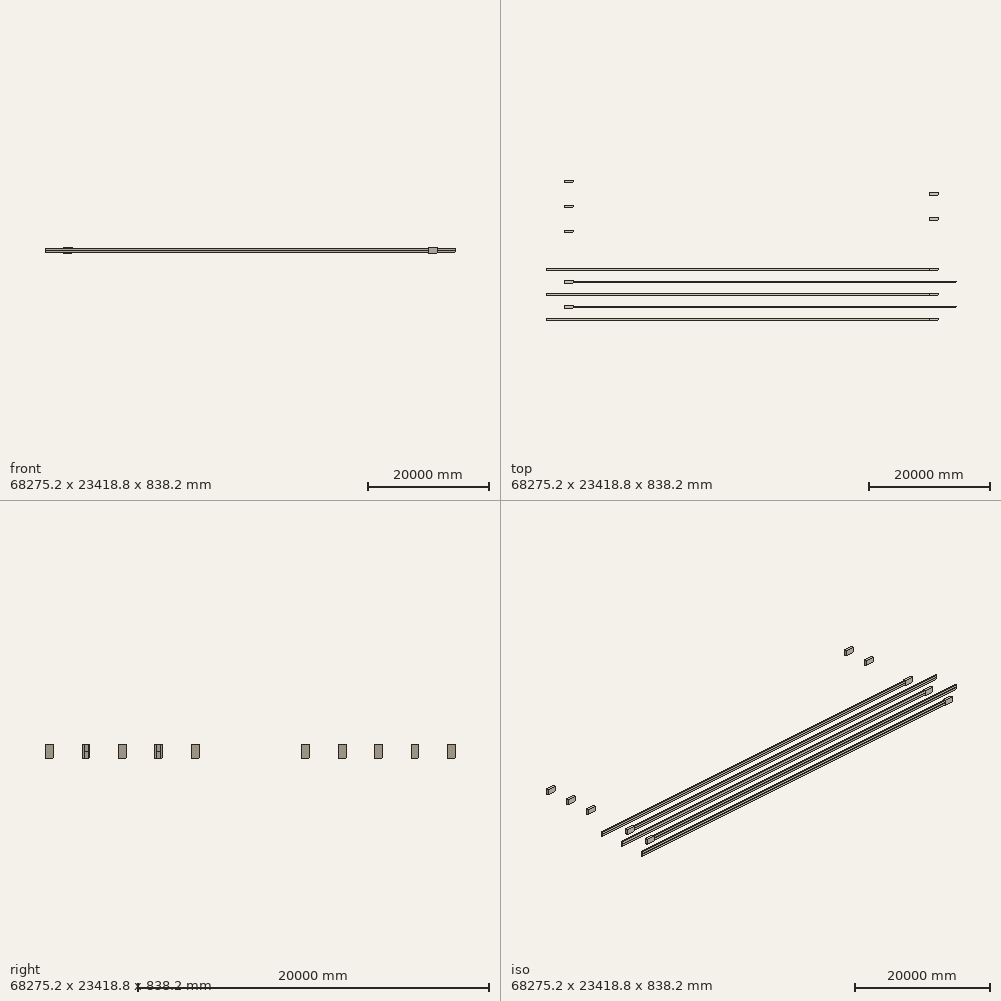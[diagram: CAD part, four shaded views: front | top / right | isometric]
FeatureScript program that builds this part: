
annotation { "Feature Type Name" : "Feature", "Feature Type Description" : "" }
export const myFeature = defineFeature(function(context is Context, id is Id, definition is map)
    precondition{}
    {
        {
            var Q0;
            Q0=qCreatedBy(makeId("Top.planeOp"),FACE);
            var sketch = newSketch(context, id + "F0", { "sketchPlane" : qUnion([Q0])});
            skLineSegment(sketch, "E0.bottom", {"start": v(-34137.6, 13411.2) * mm, "end": v(34137.6, 13411.2) * mm});
            skLineSegment(sketch, "E0.top", {"start": v(-34137.6, -13411.2) * mm, "end": v(34137.6, -13411.2) * mm});
            skLineSegment(sketch, "E0.left", {"start": v(-34137.6, 13411.2) * mm, "end": v(-34137.6, -13411.2) * mm});
            skLineSegment(sketch, "E0.right", {"start": v(34137.6, 13411.2) * mm, "end": v(34137.6, -13411.2) * mm});
            skPoint(sketch, "E0.middle", {"position": v(0, 0) * mm});
            skLineSegment(sketch, "E1", {"start": v(-31699.2, 13411.2) * mm, "end": v(-31699.2, 1219.2) * mm});
            skLineSegment(sketch, "E2", {"start": v(31699.2, 13411.2) * mm, "end": v(31699.2, 1219.2) * mm});
            skLineSegment(sketch, "E3", {"start": v(-31699.2, 1219.2) * mm, "end": v(-2438.4, 1219.2) * mm});
            skLineSegment(sketch, "E4", {"start": v(-31699.2, -1219.2) * mm, "end": v(-2438.4, -1219.2) * mm});
            skLineSegment(sketch, "E5", {"start": v(-2438.4, 13411.2) * mm, "end": v(-2438.4, 1219.2) * mm});
            skLineSegment(sketch, "E6", {"start": v(2438.4, 13411.2) * mm, "end": v(2438.4, 1219.2) * mm});
            skLineSegment(sketch, "E7.trimOffspring", {"start": v(-2438.4, -1219.2) * mm, "end": v(-2438.4, -13411.2) * mm});
            skLineSegment(sketch, "E8.trimOffspring", {"start": v(2438.4, 1219.2) * mm, "end": v(31699.2, 1219.2) * mm});
            skLineSegment(sketch, "E9.trimOffspring", {"start": v(2438.4, -1219.2) * mm, "end": v(31699.2, -1219.2) * mm});
            skLineSegment(sketch, "E10.trimOffspring", {"start": v(2438.4, -1219.2) * mm, "end": v(2438.4, -13411.2) * mm});
            skLineSegment(sketch, "E11.trimOffspring", {"start": v(-31699.2, -1219.2) * mm, "end": v(-31699.2, -13411.2) * mm});
            skLineSegment(sketch, "E12.trimOffspring", {"start": v(31699.2, -1219.2) * mm, "end": v(31699.2, -13411.2) * mm});
            skSolve(sketch);
        }
        {
            var Q0;
            {var subQ0=sQuery(id+"F0.wireOp",EDGE,"E1");Q0=makeQuery(id+"F0.imprint","IMPRINT",FACE,{"disambiguationData":[TD([[makeQuery(id+"F0.imprint","IMPRINT",EDGE,{"derivedFrom":subQ0}),1.0]])]});}
            var sketch = newSketch(context, id + "F1", { "sketchPlane" : qUnion([Q0])});
            skLineSegment(sketch, "E13.bottom", {"start": v(-31089.6, 2921) * mm, "end": v(-29616.4, 2921) * mm});
            skLineSegment(sketch, "E13.top", {"start": v(-31089.6, 3352.8) * mm, "end": v(-29616.4, 3352.8) * mm});
            skLineSegment(sketch, "E13.left", {"start": v(-31089.6, 2921) * mm, "end": v(-31089.6, 3352.8) * mm});
            skLineSegment(sketch, "E13.right", {"start": v(-29616.4, 2921) * mm, "end": v(-29616.4, 3352.8) * mm});
            skLineSegment(sketch, "E14.bottom", {"start": v(-31089.6, 7099.3) * mm, "end": v(-29616.4, 7099.3) * mm});
            skLineSegment(sketch, "E14.top", {"start": v(-31089.6, 7531.1) * mm, "end": v(-29616.4, 7531.1) * mm});
            skLineSegment(sketch, "E14.left", {"start": v(-31089.6, 7099.3) * mm, "end": v(-31089.6, 7531.1) * mm});
            skLineSegment(sketch, "E14.right", {"start": v(-29616.4, 7099.3) * mm, "end": v(-29616.4, 7531.1) * mm});
            skLineSegment(sketch, "E15.bottom", {"start": v(-31089.6, 11277.6) * mm, "end": v(-29616.4, 11277.6) * mm});
            skLineSegment(sketch, "E15.top", {"start": v(-31089.6, 11709.4) * mm, "end": v(-29616.4, 11709.4) * mm});
            skLineSegment(sketch, "E15.left", {"start": v(-31089.6, 11277.6) * mm, "end": v(-31089.6, 11709.4) * mm});
            skLineSegment(sketch, "E15.right", {"start": v(-29616.4, 11277.6) * mm, "end": v(-29616.4, 11709.4) * mm});
            skLineSegment(sketch, "E16.bottom", {"start": v(-31089.6, -9169.4) * mm, "end": v(-29616.4, -9169.4) * mm});
            skLineSegment(sketch, "E16.top", {"start": v(-31089.6, -9601.2) * mm, "end": v(-29616.4, -9601.2) * mm});
            skLineSegment(sketch, "E16.left", {"start": v(-31089.6, -9169.4) * mm, "end": v(-31089.6, -9601.2) * mm});
            skLineSegment(sketch, "E16.right", {"start": v(-29616.4, -9169.4) * mm, "end": v(-29616.4, -9601.2) * mm});
            skPoint(sketch, "E17.left.start.orphan", {"position": v(-31089.6, -5029.2) * mm});
            skLineSegment(sketch, "E18.bottom", {"start": v(-31089.6, -5029.2) * mm, "end": v(-29616.4, -5029.2) * mm});
            skLineSegment(sketch, "E18.top", {"start": v(-31089.6, -5461) * mm, "end": v(-29616.4, -5461) * mm});
            skLineSegment(sketch, "E18.left", {"start": v(-31089.6, -5029.2) * mm, "end": v(-31089.6, -5461) * mm});
            skLineSegment(sketch, "E18.right", {"start": v(-29616.4, -5029.2) * mm, "end": v(-29616.4, -5461) * mm});
            skLineSegment(sketch, "E19.bottom", {"start": v(31089.6, -7531.1) * mm, "end": v(29616.4, -7531.1) * mm});
            skLineSegment(sketch, "E19.top", {"start": v(31089.6, -7099.3) * mm, "end": v(29616.4, -7099.3) * mm});
            skLineSegment(sketch, "E19.left", {"start": v(31089.6, -7531.1) * mm, "end": v(31089.6, -7099.3) * mm});
            skLineSegment(sketch, "E19.right", {"start": v(29616.4, -7531.1) * mm, "end": v(29616.4, -7099.3) * mm});
            skLineSegment(sketch, "E20.bottom", {"start": v(31089.6, -11709.4) * mm, "end": v(29616.4, -11709.4) * mm});
            skLineSegment(sketch, "E20.top", {"start": v(31089.6, -11277.6) * mm, "end": v(29616.4, -11277.6) * mm});
            skLineSegment(sketch, "E20.left", {"start": v(31089.6, -11709.4) * mm, "end": v(31089.6, -11277.6) * mm});
            skLineSegment(sketch, "E20.right", {"start": v(29616.4, -11709.4) * mm, "end": v(29616.4, -11277.6) * mm});
            skLineSegment(sketch, "E21.bottom", {"start": v(31089.6, -3352.8) * mm, "end": v(29616.4, -3352.8) * mm});
            skLineSegment(sketch, "E21.top", {"start": v(31089.6, -2921) * mm, "end": v(29616.4, -2921) * mm});
            skLineSegment(sketch, "E21.left", {"start": v(31089.6, -3352.8) * mm, "end": v(31089.6, -2921) * mm});
            skLineSegment(sketch, "E21.right", {"start": v(29616.4, -3352.8) * mm, "end": v(29616.4, -2921) * mm});
            skPoint(sketch, "E22.oppositeSnap0", {"position": v(29616.4, -3136.9) * mm});
            skLineSegment(sketch, "E22.bottom", {"start": v(31089.6, 5029.2) * mm, "end": v(29616.4, 5029.2) * mm});
            skLineSegment(sketch, "E22.top", {"start": v(31089.6, 5461) * mm, "end": v(29616.4, 5461) * mm});
            skLineSegment(sketch, "E22.left", {"start": v(31089.6, 5029.2) * mm, "end": v(31089.6, 5461) * mm});
            skLineSegment(sketch, "E22.right", {"start": v(29616.4, 5029.2) * mm, "end": v(29616.4, 5461) * mm});
            skLineSegment(sketch, "E23.bottom", {"start": v(31089.6, 9169.4) * mm, "end": v(29616.4, 9169.4) * mm});
            skLineSegment(sketch, "E23.top", {"start": v(31089.6, 9601.2) * mm, "end": v(29616.4, 9601.2) * mm});
            skLineSegment(sketch, "E23.left", {"start": v(31089.6, 9169.4) * mm, "end": v(31089.6, 9601.2) * mm});
            skLineSegment(sketch, "E23.right", {"start": v(29616.4, 9169.4) * mm, "end": v(29616.4, 9601.2) * mm});
            skSolve(sketch);
        }
        {
            var Q0;
            Q0 = qSketchRegion(id + "F1", true);
            extrude(context, id + "F2", {"entities" : qUnion([Q0]), "depth" : 838.2 * mm, "offsetDistance" : 25.4 * mm});
        }
        {
            var Q0;
            Q0=makeQuery(id+"F2.opExtrude","SWEPT_FACE",FACE,{"disambiguationData":[OSD([sQuery(id+"F1.wireOp",EDGE,"E16.right")])]});
            var sketch = newSketch(context, id + "F3", { "sketchPlane" : qUnion([Q0])});
            skLineSegment(sketch, "E24.bottom", {"start": v(-9271, 42.33) * mm, "end": v(-9499.6, 42.33) * mm});
            skLineSegment(sketch, "E24.top", {"start": v(-9271, 397.93) * mm, "end": v(-9499.6, 397.93) * mm});
            skLineSegment(sketch, "E24.left", {"start": v(-9271, 42.33) * mm, "end": v(-9271, 397.93) * mm});
            skLineSegment(sketch, "E24.right", {"start": v(-9499.6, 42.33) * mm, "end": v(-9499.6, 397.93) * mm});
            skPoint(sketch, "E24.middle", {"position": v(-9385.3, 220.13) * mm});
            skPoint(sketch, "E24.middle.positionSnap0", {"position": v(-9385.3, 0) * mm});
            skPoint(sketch, "E24.centerSnap0", {"position": v(-9385.3, 0) * mm});
            skLineSegment(sketch, "E25.bottom", {"start": v(-9499.6, 440.27) * mm, "end": v(-9271, 440.27) * mm});
            skLineSegment(sketch, "E25.top", {"start": v(-9499.6, 795.87) * mm, "end": v(-9271, 795.87) * mm});
            skLineSegment(sketch, "E25.left", {"start": v(-9499.6, 440.27) * mm, "end": v(-9499.6, 795.87) * mm});
            skLineSegment(sketch, "E25.right", {"start": v(-9271, 440.27) * mm, "end": v(-9271, 795.87) * mm});
            skPoint(sketch, "E25.middle", {"position": v(-9385.3, 618.07) * mm});
            skLineSegment(sketch, "E26.bottom", {"start": v(-5359.4, 397.93) * mm, "end": v(-5130.8, 397.93) * mm});
            skLineSegment(sketch, "E26.top", {"start": v(-5359.4, 42.33) * mm, "end": v(-5130.8, 42.33) * mm});
            skLineSegment(sketch, "E26.left", {"start": v(-5359.4, 397.93) * mm, "end": v(-5359.4, 42.33) * mm});
            skLineSegment(sketch, "E26.right", {"start": v(-5130.8, 397.93) * mm, "end": v(-5130.8, 42.33) * mm});
            skPoint(sketch, "E26.middle", {"position": v(-5245.1, 220.13) * mm});
            skLineSegment(sketch, "E27.bottom", {"start": v(-5359.4, 440.27) * mm, "end": v(-5130.8, 440.27) * mm});
            skLineSegment(sketch, "E27.top", {"start": v(-5359.4, 795.87) * mm, "end": v(-5130.8, 795.87) * mm});
            skLineSegment(sketch, "E27.left", {"start": v(-5359.4, 440.27) * mm, "end": v(-5359.4, 795.87) * mm});
            skLineSegment(sketch, "E27.right", {"start": v(-5130.8, 440.27) * mm, "end": v(-5130.8, 795.87) * mm});
            skPoint(sketch, "E27.middle", {"position": v(-5245.1, 618.07) * mm});
            skSolve(sketch);
        }
        {
            var Q0;
            Q0 = qSketchRegion(id + "F3", true);
            extrude(context, id + "F4", {"entities" : qUnion([Q0]), "depth" : 63754 * mm, "offsetDistance" : 25.4 * mm});
        }
        {
            var Q0;
            Q0=makeQuery(id+"F2.opExtrude","SWEPT_FACE",FACE,{"disambiguationData":[OSD([sQuery(id+"F1.wireOp",EDGE,"E21.right")])]});
            var sketch = newSketch(context, id + "F5", { "sketchPlane" : qUnion([Q0])});
            skLineSegment(sketch, "E28.bottom", {"start": v(3022.6, 397.93) * mm, "end": v(3251.2, 397.93) * mm});
            skLineSegment(sketch, "E28.top", {"start": v(3022.6, 42.33) * mm, "end": v(3251.2, 42.33) * mm});
            skLineSegment(sketch, "E28.left", {"start": v(3022.6, 397.93) * mm, "end": v(3022.6, 42.33) * mm});
            skLineSegment(sketch, "E28.right", {"start": v(3251.2, 397.93) * mm, "end": v(3251.2, 42.33) * mm});
            skPoint(sketch, "E28.middle", {"position": v(3136.9, 220.13) * mm});
            skPoint(sketch, "E28.middle.positionSnap0", {"position": v(3136.9, 0) * mm});
            skPoint(sketch, "E28.centerSnap0", {"position": v(3136.9, 0) * mm});
            skLineSegment(sketch, "E29.bottom", {"start": v(3022.6, 440.27) * mm, "end": v(3251.2, 440.27) * mm});
            skLineSegment(sketch, "E29.top", {"start": v(3022.6, 795.87) * mm, "end": v(3251.2, 795.87) * mm});
            skLineSegment(sketch, "E29.left", {"start": v(3022.6, 440.27) * mm, "end": v(3022.6, 795.87) * mm});
            skLineSegment(sketch, "E29.right", {"start": v(3251.2, 440.27) * mm, "end": v(3251.2, 795.87) * mm});
            skPoint(sketch, "E29.middle", {"position": v(3136.9, 618.07) * mm});
            skLineSegment(sketch, "E30.bottom", {"start": v(7200.9, 397.93) * mm, "end": v(7429.5, 397.93) * mm});
            skLineSegment(sketch, "E30.top", {"start": v(7200.9, 42.33) * mm, "end": v(7429.5, 42.33) * mm});
            skLineSegment(sketch, "E30.left", {"start": v(7200.9, 397.93) * mm, "end": v(7200.9, 42.33) * mm});
            skLineSegment(sketch, "E30.right", {"start": v(7429.5, 397.93) * mm, "end": v(7429.5, 42.33) * mm});
            skPoint(sketch, "E30.middle", {"position": v(7315.2, 220.13) * mm});
            skLineSegment(sketch, "E31.bottom", {"start": v(7200.9, 795.87) * mm, "end": v(7429.5, 795.87) * mm});
            skLineSegment(sketch, "E31.top", {"start": v(7200.9, 440.27) * mm, "end": v(7429.5, 440.27) * mm});
            skLineSegment(sketch, "E31.left", {"start": v(7200.9, 795.87) * mm, "end": v(7200.9, 440.27) * mm});
            skLineSegment(sketch, "E31.right", {"start": v(7429.5, 795.87) * mm, "end": v(7429.5, 440.27) * mm});
            skPoint(sketch, "E31.middle", {"position": v(7315.2, 618.07) * mm});
            skLineSegment(sketch, "E32.bottom", {"start": v(11379.2, 397.93) * mm, "end": v(11607.8, 397.93) * mm});
            skLineSegment(sketch, "E32.top", {"start": v(11379.2, 42.33) * mm, "end": v(11607.8, 42.33) * mm});
            skLineSegment(sketch, "E32.left", {"start": v(11379.2, 397.93) * mm, "end": v(11379.2, 42.33) * mm});
            skLineSegment(sketch, "E32.right", {"start": v(11607.8, 397.93) * mm, "end": v(11607.8, 42.33) * mm});
            skPoint(sketch, "E32.middle", {"position": v(11493.5, 220.13) * mm});
            skLineSegment(sketch, "E33.bottom", {"start": v(11379.2, 440.27) * mm, "end": v(11607.8, 440.27) * mm});
            skLineSegment(sketch, "E33.top", {"start": v(11379.2, 795.87) * mm, "end": v(11607.8, 795.87) * mm});
            skLineSegment(sketch, "E33.left", {"start": v(11379.2, 440.27) * mm, "end": v(11379.2, 795.87) * mm});
            skLineSegment(sketch, "E33.right", {"start": v(11607.8, 440.27) * mm, "end": v(11607.8, 795.87) * mm});
            skPoint(sketch, "E33.middle", {"position": v(11493.5, 618.07) * mm});
            skSolve(sketch);
        }
        {
            var Q0;
            Q0 = qSketchRegion(id + "F5", true);
            extrude(context, id + "F6", {"entities" : qUnion([Q0]), "depth" : 63754 * mm, "offsetDistance" : 25.4 * mm});
        }
    });
